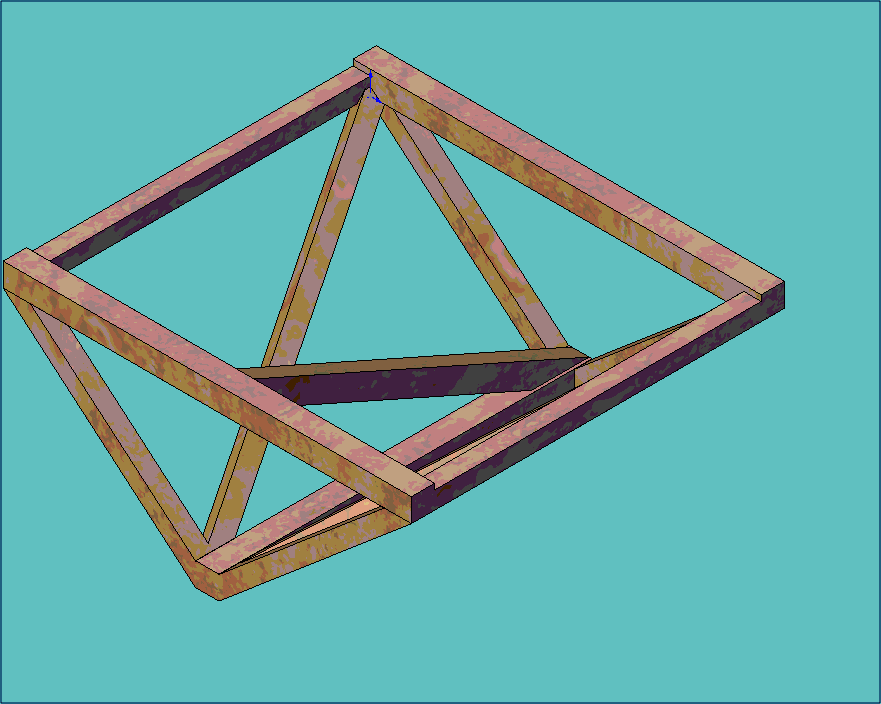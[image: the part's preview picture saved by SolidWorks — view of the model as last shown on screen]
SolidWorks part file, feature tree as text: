
SOLIDWORKS PART (.sldprt)
format: sldprt  version: not decoded by parser v0  size: 496,128 bytes
history: native  units: mm
features: sketch x8, extrude x8, plane x2, material x1, shell x1 (+11 scaffold rows collapsed)
feature tree (31):
  scaffold x11  (default folders/planes/origin — collapsed)
  material  "Material <not specified>"
  sketch  "Sketch1"  dims[D1=101.6mm D2=4.7625mm D3=6.35mm D4=101.6mm D5=4.7625mm]
  extrude  "Wing Main Bars"  Depth=6.35mm
  extrude  "Wing Crossabrs"  [1 undecoded]
  sketch  "Sketch1<3>"  dims[D1=4.7625mm]
  shell  "Hollow out wing"  Thickness=0.00254mm
  plane  "Bottom"  Offset=38.1mm
  sketch  "Sketch2"  dims[D1=6.35mm D2=25.4mm]
  extrude  "Plane Body"  Depth=6.35mm
  plane  "Center"
  sketch  "Sketch8"  dims[D1=6.35mm]
  extrude  "Extrude7"  Depth=4.7625mm
  sketch  "Sketch9"  dims[c1.D1=4.7625mm c1.D2=4.7625mm c2.D1=4.7625mm]
  extrude  "Extrude8"  Depth=4.7625mm
  sketch  "Sketch11"  dims[D1=4.7625mm]
  extrude  "Extrude9"  Depth=4.7625mm
  sketch  "Sketch12"  dims[D1=4.7625mm]
  extrude  "Extrude10"  Depth=4.7625mm
  sketch  "Sketch13"  dims[D1=4.7625mm]
  extrude  "Extrude11"  Depth=4.7625mm
decode coverage: 16 of 17 modeling features carry decoded parameters
note: 1 parameter value undecoded
note: suppression state not decoded; provenance and decode notes live in map.json
